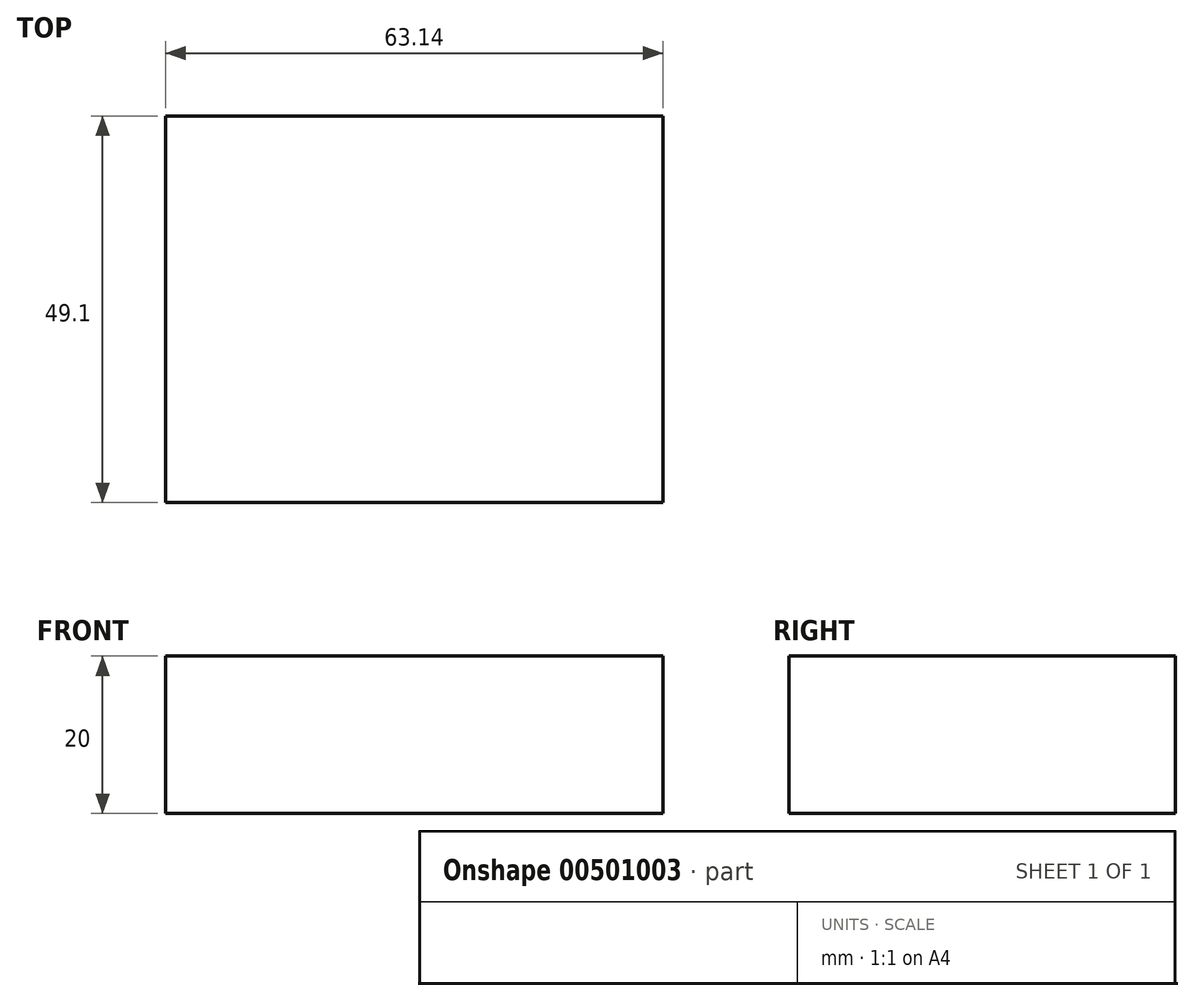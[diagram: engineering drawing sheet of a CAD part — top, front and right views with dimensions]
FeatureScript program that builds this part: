
annotation { "Feature Type Name" : "Feature", "Feature Type Description" : "" }
export const myFeature = defineFeature(function(context is Context, id is Id, definition is map)
    precondition{}
    {
        {
            var Q0;
            Q0=qCreatedBy(makeId("Top.planeOp"),FACE);
            var sketch = newSketch(context, id + "F0", { "sketchPlane" : qUnion([Q0])});
            skLineSegment(sketch, "E0.bottom", {"start": v(31.57, 24.55) * mm, "end": v(-31.57, 24.55) * mm});
            skLineSegment(sketch, "E0.top", {"start": v(31.57, -24.55) * mm, "end": v(-31.57, -24.55) * mm});
            skLineSegment(sketch, "E0.left", {"start": v(31.57, 24.55) * mm, "end": v(31.57, -24.55) * mm});
            skLineSegment(sketch, "E0.right", {"start": v(-31.57, 24.55) * mm, "end": v(-31.57, -24.55) * mm});
            skPoint(sketch, "E0.middle", {"position": v(0, 0) * mm});
            skSolve(sketch);
        }
        {
            var Q0;
            Q0=makeQuery(id+"F0.imprint","IMPRINT",FACE,{"disambiguationData":[TD([[makeQuery(id+"F0.imprint","IMPRINT",EDGE,{"derivedFrom":sQuery(id+"F0.wireOp",EDGE,"E0.bottom")}),1.0]])]});
            extrude(context, id + "F1", {"entities" : qUnion([Q0]), "depth" : 20 * mm, "offsetDistance" : 25 * mm});
        }
    });
